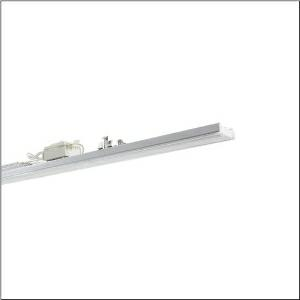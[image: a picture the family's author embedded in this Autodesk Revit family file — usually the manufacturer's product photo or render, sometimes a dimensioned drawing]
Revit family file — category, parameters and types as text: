
# Revit family: licross_r__21_recessed_ho_52tl1edn4dxs_e230
name_source: partatom
category: Lighting Fixtures
units: mm (PartAtom-declared; Revit-internal decimal feet)

## family parameters
Cut with Voids When Loaded = No
Host = Face
Light Source = No
Part Type = Normal
Room Calculation Point = No
Round Connector Dimension = Use Diameter
Shared = No

## types (1)
- --- (1 x LED, 13000 lm, 74.4 W, 4000K)
    Apparent Load = 74 VA
    CIE Flux Codes = 85 95 99 100 100
    Color Rendering = 80
    Color Temperature = 4000K
    Default Elevation = 1800 mm
    Description = Licross® 21 Recessed HO, luminaire insert, of sheet steel, galvanised, coil coated, white, length: 1.500mm, width: 66mm, height: 67mm, LED rated luminous flux: 13.000lm, light colour: 840, control gear: DALI 2, with plug, 5-pole, with phase selection, mains connection: 220..240V, AC, 50/60Hz, rated input power: 74W, halogen-free wiring, primary light control with lens, of plastic, primary optical cover: cover, of PMMA, light emission: direct distribution, primary light characteristic: symmetric, protection rating (complete): IP40, insulation class (complete): insulation class I (protective earthing), certification: CE, ENEC, VDE, UKCA, protection symbol: D if used in an environment without relevant dust loads with corresponding accessories, impact resistance: IK06, permissible ambient temperature for indoor applications: -25..+30°C, corresponds to IFS (International Featured Standards) requirements for safety and quality in the food industry, reducing of maximum allowable ambient temperature of 5°C with ceiling mounting, LABS conformity tested according to VDMA 24364:2018-05, packaging unit: 1 piece
    Height = 58 mm
    Lamp = 1 x LED
    Lamp Light Flux = 13000 lm
    Lamp Power = 74.4 W
    Lamp count = 1
    Length = 1500 mm
    Luminous efficacy = 175 lm/W
    Manufacturer = Siteco
    ModVariant = No
    Model = 52TL1EDN4DXS
    Mounting Place = Ceiling
    Mounting Type = Pendant
    Number of Poles = 1
    OnlyDefault = Yes
    Power Factor = 1
    Product Name = Licross® 21 Recessed HO
    Product group = luminaire insert
    ProductGroupID = 902
    Protection Class = Protection class I
    Protection Degree = IP 40
    RLX_Detail_Level = 1
    RLX_Emergency_Light_Flux = 0 lm
    RLX_Emergency_Type = 0
    RLX_Emergency_Type_DB = No
    RlxData = <blob elided: 24649 chars, md5=c1a6d3e6>
    Socket = socket
    Standby Power = 0 W
    System Light Flux = 13000 lm
    System Power = 74 W
    Type Comments = factory setting: luminous flux: 100 % | dim-lin: 254 | 426 mA
    Type Image = l_1296930.jpg
    URL = http://relux.com
    VarID = @adj_125096
    Voltage = 0 V
    Weight = 0.00 kg
    Width = 66 mm

## geometry (parser evidence)
native form markers: Blend x4, Sweep x10
no freeform markers — native parametric forms only
